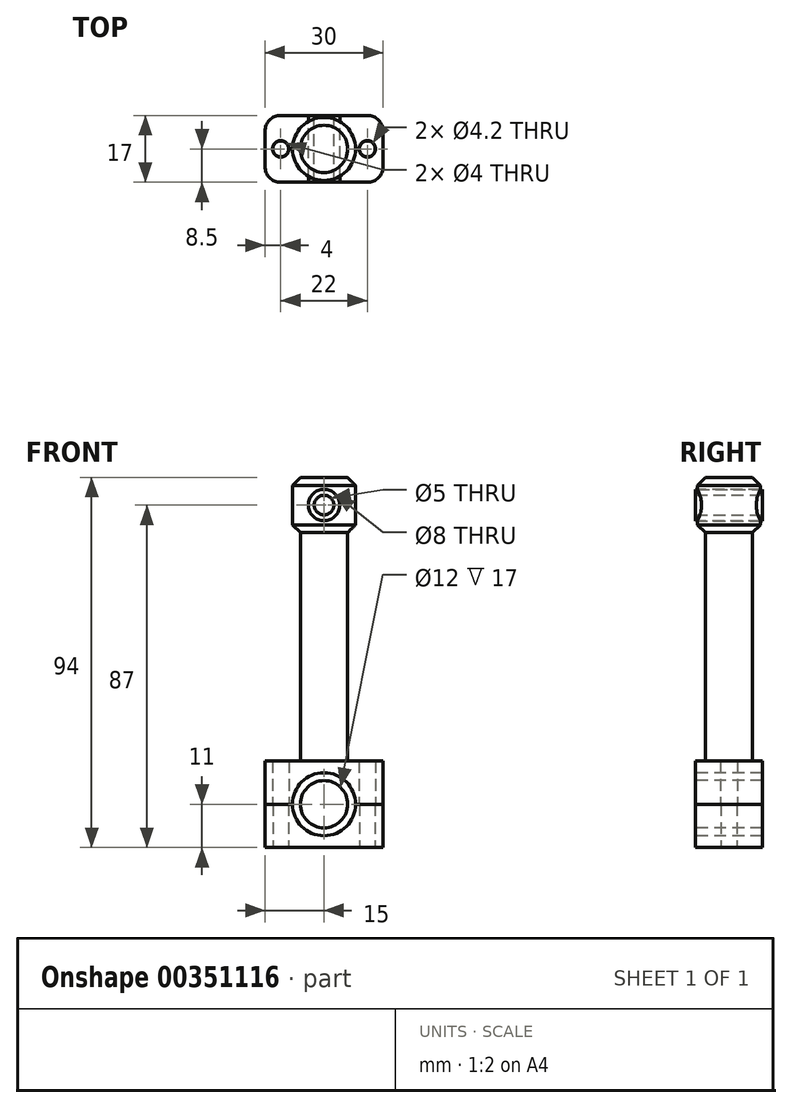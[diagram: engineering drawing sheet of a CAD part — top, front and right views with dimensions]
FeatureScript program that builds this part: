
annotation { "Feature Type Name" : "Feature", "Feature Type Description" : "" }
export const myFeature = defineFeature(function(context is Context, id is Id, definition is map)
    precondition{}
    {
        {
            var Q0;
            Q0=qCreatedBy(makeId("Top.planeOp"),FACE);
            var sketch = newSketch(context, id + "F0", { "sketchPlane" : qUnion([Q0])});
            skLineSegment(sketch, "E0.bottom", {"start": v(11, -8.5) * mm, "end": v(-11, -8.5) * mm});
            skLineSegment(sketch, "E0.top", {"start": v(11, 8.5) * mm, "end": v(-11, 8.5) * mm});
            skLineSegment(sketch, "E0.left", {"start": v(15, -4.5) * mm, "end": v(15, 4.5) * mm});
            skLineSegment(sketch, "E0.right", {"start": v(-15, -4.5) * mm, "end": v(-15, 4.5) * mm});
            skPoint(sketch, "E0.middle", {"position": v(0, 0) * mm});
            skPoint(sketch, "E1.visualSharp", {"position": v(-15, 8.5) * mm});
            skArc(sketch, "E1.filletArc", {"start": v(-11, 8.5) * mm, "mid": v(-13.83, 7.33) * mm, "end": v(-15, 4.5) * mm});
            skPoint(sketch, "E2.visualSharp", {"position": v(-15, -8.5) * mm});
            skArc(sketch, "E2.filletArc", {"start": v(-15, -4.5) * mm, "mid": v(-13.83, -7.33) * mm, "end": v(-11, -8.5) * mm});
            skPoint(sketch, "E3.visualSharp", {"position": v(15, -8.5) * mm});
            skArc(sketch, "E3.filletArc", {"start": v(11, -8.5) * mm, "mid": v(13.83, -7.33) * mm, "end": v(15, -4.5) * mm});
            skPoint(sketch, "E4.visualSharp", {"position": v(15, 8.5) * mm});
            skArc(sketch, "E4.filletArc", {"start": v(15, 4.5) * mm, "mid": v(13.83, 7.33) * mm, "end": v(11, 8.5) * mm});
            skCircle(sketch, "E5", {"center": v(-11, 0) * mm, "radius": 2 * mm});
            skCircle(sketch, "E6", {"center": v(11, 0) * mm, "radius": 2 * mm});
            skSolve(sketch);
        }
        {
            var Q0;
            Q0=makeQuery(id+"F0.imprint","IMPRINT",FACE,{"disambiguationData":[TD([[makeQuery(id+"F0.imprint","IMPRINT",EDGE,{"derivedFrom":sQuery(id+"F0.wireOp",EDGE,"E0.bottom")}),-1.0]])]});
            extrude(context, id + "F1", {"entities" : qUnion([Q0]), "depth" : 11 * mm});
        }
        {
            var Q0;
            Q0=makeQuery(id+"F1.opExtrude","CAP_FACE",FACE,{"disambiguationData":[OSD([sQuery(id+"F0.wireOp",EDGE,"E0.bottom"),sQuery(id+"F0.wireOp",EDGE,"E0.top"),sQuery(id+"F0.wireOp",EDGE,"E0.left"),sQuery(id+"F0.wireOp",EDGE,"E0.right"),sQuery(id+"F0.wireOp",EDGE,"E1.filletArc"),sQuery(id+"F0.wireOp",EDGE,"E2.filletArc"),sQuery(id+"F0.wireOp",EDGE,"E3.filletArc"),sQuery(id+"F0.wireOp",EDGE,"E4.filletArc"),sQuery(id+"F0.wireOp",EDGE,"E5"),sQuery(id+"F0.wireOp",EDGE,"E6")])],"isStart":false});
            var sketch = newSketch(context, id + "F2", { "sketchPlane" : qUnion([Q0])});
            skPoint(sketch, "E7", {"position": v(-11, 0) * mm});
            skPoint(sketch, "E8", {"position": v(11, 0) * mm});
            skSolve(sketch);
        }
        {
            var Q0;
            Q0=makeQuery(id+"F2.imprint","IMPRINT",FACE,{"disambiguationData":[TD([[makeQuery(id+"F2.imprint","IMPRINT",EDGE,{"derivedFrom":makeQuery(id+"F1.opExtrude","CAP_EDGE",EDGE,{"disambiguationData":[OSD([sQuery(id+"F0.wireOp",EDGE,"E0.bottom")])],"isStart":false})}),-1.0]])]});
            var Q1;
            Q1=makeQuery(id+"F2.imprint","IMPRINT",FACE,{"disambiguationData":[TD([[makeQuery(id+"F2.imprint","IMPRINT",EDGE,{"derivedFrom":makeQuery(id+"F1.opExtrude","CAP_EDGE",EDGE,{"disambiguationData":[OSD([sQuery(id+"F0.wireOp",EDGE,"E5")])],"isStart":false})}),1.0]])]});
            var Q2;
            Q2=makeQuery(id+"F2.imprint","IMPRINT",FACE,{"disambiguationData":[TD([[makeQuery(id+"F2.imprint","IMPRINT",EDGE,{"derivedFrom":makeQuery(id+"F1.opExtrude","CAP_EDGE",EDGE,{"disambiguationData":[OSD([sQuery(id+"F0.wireOp",EDGE,"E6")])],"isStart":false})}),1.0]])]});
            extrude(context, id + "F3", {"entities" : qUnion([Q0, Q1, Q2]), "depth" : 11 * mm});
        }
        {
            var Q0;
            Q0=sQuery(id+"F2.wireOp",VERTEX,"E7");
            var Q1;
            Q1=sQuery(id+"F2.wireOp",VERTEX,"E8");
            var Q2;
            Q2=makeQuery(id+"F3.opExtrude","SWEPT_BODY",BODY,{"disambiguationData":[OSD([sQuery(id+"F0.wireOp",EDGE,"E0.bottom"),sQuery(id+"F0.wireOp",EDGE,"E0.top"),sQuery(id+"F0.wireOp",EDGE,"E0.left"),sQuery(id+"F0.wireOp",EDGE,"E0.right"),sQuery(id+"F0.wireOp",EDGE,"E1.filletArc"),sQuery(id+"F0.wireOp",EDGE,"E2.filletArc"),sQuery(id+"F0.wireOp",EDGE,"E3.filletArc"),sQuery(id+"F0.wireOp",EDGE,"E4.filletArc")])]});
            hole(context, id + "F4", {"style" : HoleStyle.SIMPLE, "endStyle" : HoleEndStyle.THROUGH, "oppositeDirection" : true, "standardTappedOrClearance" : lookupTablePath({ "standard" : "ISO", "engagement" : "75%", "pitch" : "0.8 mm", "size" : "M5", "type" : "Tapped" }), "standardBlindInLast" : lookupTablePath({ "standard" : "ISO", "engagement" : "75%", "pitch" : "0.8 mm", "size" : "M5", "type" : "Tapped" }), "holeDiameter" : 4.2 * mm, "showTappedDepth" : true, "isTappedThrough" : true, "tappedDepth" : 10 * mm, "tapClearance" : 1, "locations" : qUnion([Q0, Q1]), "scope" : qUnion([Q2]), "majorDiameter" : 5 * mm});
        }
        {
            var Q0;
            Q0=makeQuery(id+"F3.opExtrude","CAP_FACE",FACE,{"disambiguationData":[OSD([sQuery(id+"F0.wireOp",EDGE,"E0.bottom"),sQuery(id+"F0.wireOp",EDGE,"E0.top"),sQuery(id+"F0.wireOp",EDGE,"E0.left"),sQuery(id+"F0.wireOp",EDGE,"E0.right"),sQuery(id+"F0.wireOp",EDGE,"E1.filletArc"),sQuery(id+"F0.wireOp",EDGE,"E2.filletArc"),sQuery(id+"F0.wireOp",EDGE,"E3.filletArc"),sQuery(id+"F0.wireOp",EDGE,"E4.filletArc")])],"isStart":false});
            var sketch = newSketch(context, id + "F5", { "sketchPlane" : qUnion([Q0])});
            skCircle(sketch, "E9", {"center": v(0, 0) * mm, "radius": 6 * mm});
            skSolve(sketch);
        }
        {
            var Q0;
            Q0=makeQuery(id+"F5.imprint","IMPRINT",FACE,{"disambiguationData":[TD([[makeQuery(id+"F5.imprint","IMPRINT",EDGE,{"derivedFrom":sQuery(id+"F5.wireOp",EDGE,"E9")}),1.0]])]});
            extrude(context, id + "F6", {"entities" : qUnion([Q0]), "operationType" : NewBodyOperationType.ADD, "depth" : 58 * mm});
        }
        {
            var Q0;
            Q0=makeQuery(id+"F6.opExtrude","CAP_FACE",FACE,{"disambiguationData":[OSD([sQuery(id+"F5.wireOp",EDGE,"E9")])],"isStart":false});
            var sketch = newSketch(context, id + "F7", { "sketchPlane" : qUnion([Q0])});
            skCircle(sketch, "E10", {"center": v(0, 0) * mm, "radius": 8 * mm});
            skSolve(sketch);
        }
        {
            var Q0;
            Q0=makeQuery(id+"F7.imprint","IMPRINT",FACE,{"disambiguationData":[TD([[makeQuery(id+"F7.imprint","IMPRINT",EDGE,{"derivedFrom":sQuery(id+"F7.wireOp",EDGE,"E10")}),1.0]])]});
            var Q1;
            Q1=makeQuery(id+"F7.imprint","IMPRINT",FACE,{"disambiguationData":[TD([[makeQuery(id+"F7.imprint","IMPRINT",EDGE,{"derivedFrom":makeQuery(id+"F6.opExtrude","CAP_EDGE",EDGE,{"disambiguationData":[OSD([sQuery(id+"F5.wireOp",EDGE,"E9")])],"isStart":false})}),1.0]])]});
            extrude(context, id + "F8", {"entities" : qUnion([Q0, Q1]), "operationType" : NewBodyOperationType.ADD, "depth" : 14 * mm});
        }
        {
            var Q0;
            Q0=makeQuery(id+"F8.opExtrude","CAP_EDGE",EDGE,{"disambiguationData":[OSD([sQuery(id+"F7.wireOp",EDGE,"E10")])],"isStart":true});
            var Q1;
            Q1=makeQuery(id+"F8.opExtrude","CAP_EDGE",EDGE,{"disambiguationData":[OSD([sQuery(id+"F7.wireOp",EDGE,"E10")])],"isStart":false});
            chamfer(context, id + "F9", {"entities" : qUnion([Q0, Q1]), "width" : 2 * mm, "tangentPropagation" : true});
        }
        {
            var Q0;
            Q0=makeQuery(id+"F3.opExtrude","SWEPT_FACE",FACE,{"disambiguationData":[OSD([sQuery(id+"F0.wireOp",EDGE,"E0.bottom")])]});
            var sketch = newSketch(context, id + "F10", { "sketchPlane" : qUnion([Q0])});
            skCircle(sketch, "E11", {"center": v(0, 11) * mm, "radius": 6 * mm});
            skCircle(sketch, "E12", {"center": v(0, 11) * mm, "radius": 8 * mm});
            skSolve(sketch);
        }
        {
            var Q0;
            {var subQ0=sQuery(id+"F10.wireOp",EDGE,"E11");var subQ1=makeQuery(id+"F3.opExtrude","CAP_EDGE",EDGE,{"disambiguationData":[OSD([sQuery(id+"F0.wireOp",EDGE,"E0.bottom")])],"isStart":true});var subQ2=makeQuery(id+"F10.imprint","INTERSECT",VERTEX,{"disambiguationData":[OD(0.0)],"derivedFrom":[subQ1,subQ0]});Q0=makeQuery(id+"F10.imprint","IMPRINT",FACE,{"disambiguationData":[TD([[makeQuery(id+"F10.imprint","IMPRINT",EDGE,{"disambiguationData":[TD([[subQ2,-1.0]])],"derivedFrom":subQ0}),1.0]])]});}
            var Q1;
            {var subQ0=sQuery(id+"F10.wireOp",EDGE,"E11");var subQ1=makeQuery(id+"F3.opExtrude","CAP_EDGE",EDGE,{"disambiguationData":[OSD([sQuery(id+"F0.wireOp",EDGE,"E0.bottom")])],"isStart":true});var subQ2=makeQuery(id+"F10.imprint","INTERSECT",VERTEX,{"disambiguationData":[OD(0.0)],"derivedFrom":[subQ1,subQ0]});Q1=makeQuery(id+"F10.imprint","IMPRINT",FACE,{"disambiguationData":[TD([[makeQuery(id+"F10.imprint","IMPRINT",EDGE,{"disambiguationData":[TD([[subQ2,-1.0]])],"derivedFrom":subQ0}),-1.0]])]});}
            var Q2;
            {var subQ0=sQuery(id+"F10.wireOp",EDGE,"E11");var subQ1=makeQuery(id+"F3.opExtrude","CAP_EDGE",EDGE,{"disambiguationData":[OSD([sQuery(id+"F0.wireOp",EDGE,"E0.bottom")])],"isStart":true});var subQ2=makeQuery(id+"F10.imprint","INTERSECT",VERTEX,{"disambiguationData":[OD(0.0)],"derivedFrom":[subQ1,subQ0]});Q2=makeQuery(id+"F10.imprint","IMPRINT",FACE,{"disambiguationData":[TD([[makeQuery(id+"F10.imprint","IMPRINT",EDGE,{"disambiguationData":[TD([[subQ2,1.0]])],"derivedFrom":subQ0}),-1.0]])]});}
            var Q3;
            {var subQ0=sQuery(id+"F10.wireOp",EDGE,"E11");var subQ1=makeQuery(id+"F3.opExtrude","CAP_EDGE",EDGE,{"disambiguationData":[OSD([sQuery(id+"F0.wireOp",EDGE,"E0.bottom")])],"isStart":true});var subQ2=makeQuery(id+"F10.imprint","INTERSECT",VERTEX,{"disambiguationData":[OD(0.0)],"derivedFrom":[subQ1,subQ0]});Q3=makeQuery(id+"F10.imprint","IMPRINT",FACE,{"disambiguationData":[TD([[makeQuery(id+"F10.imprint","IMPRINT",EDGE,{"disambiguationData":[TD([[subQ2,1.0]])],"derivedFrom":subQ0}),1.0]])]});}
            extrude(context, id + "F11", {"entities" : qUnion([Q0, Q1, Q2, Q3]), "operationType" : NewBodyOperationType.REMOVE, "endBound" : BoundingType.THROUGH_ALL, "oppositeDirection" : true, "depth" : 25 * mm});
        }
        {
            var Q0;
            {var subQ0=sQuery(id+"F10.wireOp",EDGE,"E11");var subQ1=makeQuery(id+"F3.opExtrude","CAP_EDGE",EDGE,{"disambiguationData":[OSD([sQuery(id+"F0.wireOp",EDGE,"E0.bottom")])],"isStart":true});var subQ2=makeQuery(id+"F10.imprint","INTERSECT",VERTEX,{"disambiguationData":[OD(0.0)],"derivedFrom":[subQ1,subQ0]});Q0=makeQuery(id+"F10.imprint","IMPRINT",FACE,{"disambiguationData":[TD([[makeQuery(id+"F10.imprint","IMPRINT",EDGE,{"disambiguationData":[TD([[subQ2,1.0]])],"derivedFrom":subQ0}),-1.0]])]});}
            var Q1;
            {var subQ0=sQuery(id+"F10.wireOp",EDGE,"E11");var subQ1=makeQuery(id+"F3.opExtrude","CAP_EDGE",EDGE,{"disambiguationData":[OSD([sQuery(id+"F0.wireOp",EDGE,"E0.bottom")])],"isStart":true});var subQ2=makeQuery(id+"F10.imprint","INTERSECT",VERTEX,{"disambiguationData":[OD(0.0)],"derivedFrom":[subQ1,subQ0]});Q1=makeQuery(id+"F10.imprint","IMPRINT",FACE,{"disambiguationData":[TD([[makeQuery(id+"F10.imprint","IMPRINT",EDGE,{"disambiguationData":[TD([[subQ2,-1.0]])],"derivedFrom":subQ0}),-1.0]])]});}
            extrude(context, id + "F12", {"entities" : qUnion([Q0, Q1]), "oppositeDirection" : true, "depth" : 17 * mm});
        }
        {
            var Q0;
            Q0=qCreatedBy(makeId("Front.planeOp"),FACE);
            var sketch = newSketch(context, id + "F13", { "sketchPlane" : qUnion([Q0])});
            skCircle(sketch, "E13", {"center": v(0, 87) * mm, "radius": 2.5 * mm});
            skCircle(sketch, "E14", {"center": v(0, 87) * mm, "radius": 4 * mm});
            skSolve(sketch);
        }
        {
            var Q0;
            Q0=makeQuery(id+"F13.imprint","IMPRINT",FACE,{"disambiguationData":[TD([[makeQuery(id+"F13.imprint","IMPRINT",EDGE,{"derivedFrom":sQuery(id+"F13.wireOp",EDGE,"E13")}),-1.0]])]});
            var Q1;
            Q1=makeQuery(id+"F13.imprint","IMPRINT",FACE,{"disambiguationData":[TD([[makeQuery(id+"F13.imprint","IMPRINT",EDGE,{"derivedFrom":sQuery(id+"F13.wireOp",EDGE,"E13")}),1.0]])]});
            extrude(context, id + "F14", {"entities" : qUnion([Q0, Q1]), "operationType" : NewBodyOperationType.REMOVE, "endBound" : BoundingType.THROUGH_ALL, "oppositeDirection" : true, "depth" : 25 * mm, "hasSecondDirection" : true, "secondDirectionBound" : SecondDirectionBoundingType.THROUGH_ALL, "secondDirectionOppositeDirection" : false, "secondDirectionDepth" : 25 * mm});
        }
        {
            var Q0;
            Q0=makeQuery(id+"F13.imprint","IMPRINT",FACE,{"disambiguationData":[TD([[makeQuery(id+"F13.imprint","IMPRINT",EDGE,{"derivedFrom":sQuery(id+"F13.wireOp",EDGE,"E13")}),-1.0]])]});
            extrude(context, id + "F15", {"entities" : qUnion([Q0]), "endBound" : BoundingType.SYMMETRIC, "depth" : 17 * mm});
        }
    });
